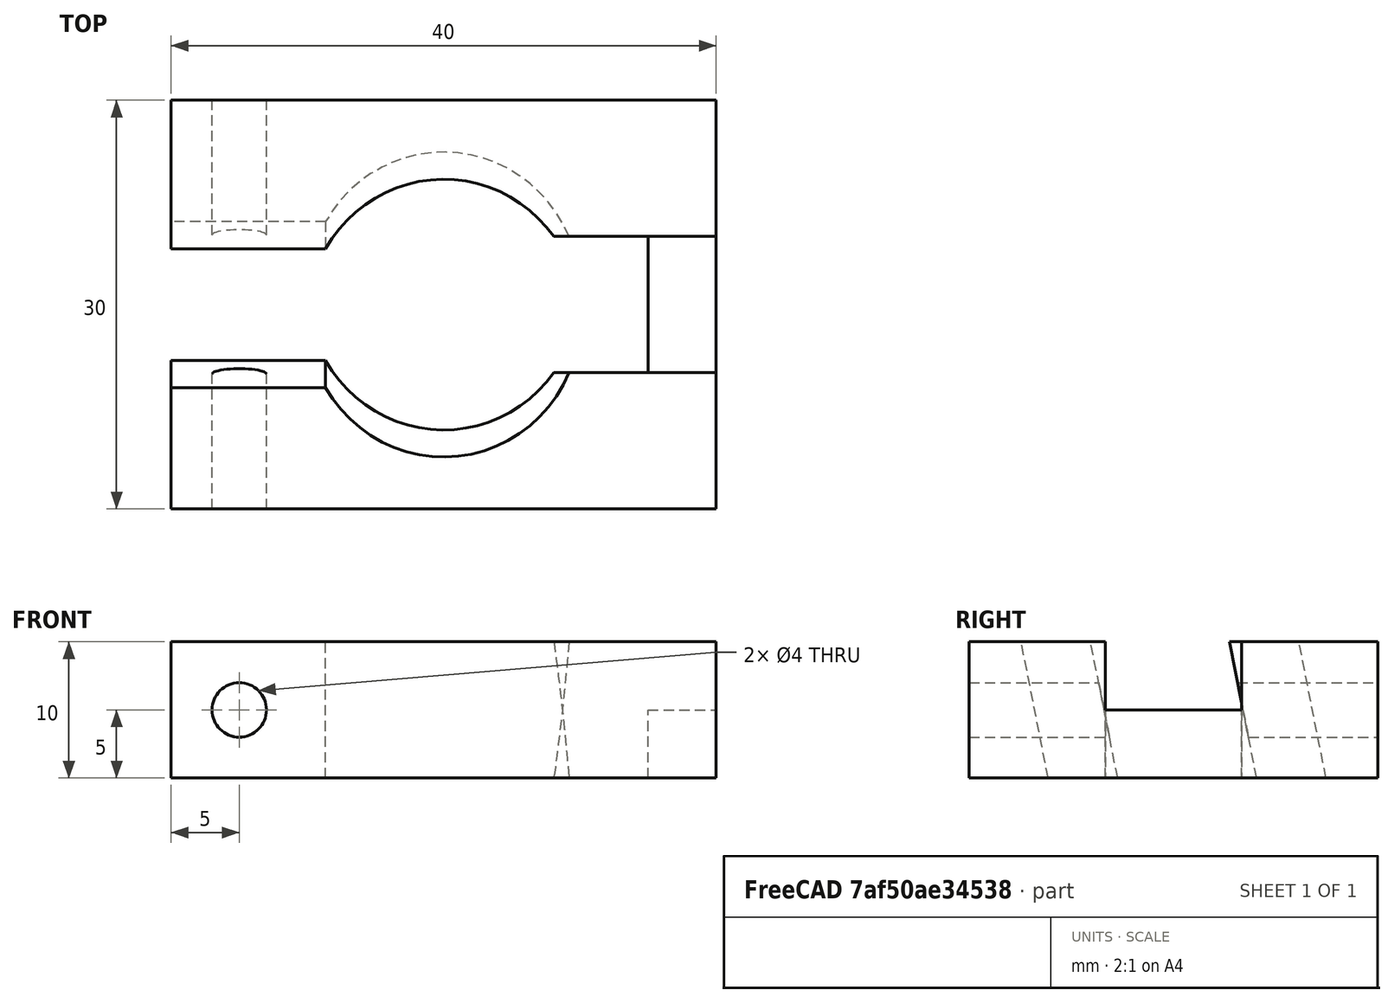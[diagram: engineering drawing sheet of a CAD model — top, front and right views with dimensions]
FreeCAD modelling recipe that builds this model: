
FCSTD DOCUMENT  (FreeCAD 0.17R13522 (Git))
Label: fastener-middleturn-rev-20mm
License: All rights reserved
LicenseURL: http://en.wikipedia.org/wiki/All_rights_reserved
objects: Part::Box×4, Part::Cylinder×2, Part::MultiFuse×2, Part::Cut×1
note: 9 computed .brp shape members not serialized (recipe doc carries the construction recipe); baked Part::Feature solids carry a one-line shape summary decoded from their .brp

FEATURE [Part::Box] Box  label="Cube"
  AttacherType = Attacher::AttachEngine3D
  Height = 10
  Length = 40
  Placement = pos=(-20,-15,-5) rot=(0,0,1;0rad)
  Width = 30
FEATURE [Part::Box] Box001  label="Cube001"
  AttacherType = Attacher::AttachEngine3D
  Height = 10
  Length = 10
  Placement = pos=(5,-5,-5) rot=(0,0,1;0rad)
  Width = 10
FEATURE [Part::Box] Box002  label="Cube002"
  AttacherType = Attacher::AttachEngine3D
  Height = 5
  Length = 10
  Placement = pos=(10,-5,0) rot=(0,0,1;0rad)
  Width = 10
FEATURE [Part::Cylinder] Cylinder003
  Angle = 360
  AttacherType = Attacher::AttachEngine3D
  Height = 30
  Placement = pos=(-15,-15,0) rot=(-1,0,0;1.5708rad)
  Radius = 2
FEATURE [Part::Box] Box003  label="Squeeze Cube"
  AttacherType = Attacher::AttachEngine3D
  Height = 20
  Length = 15
  Placement = pos=(-20,-5,-10) rot=(0,0,1;0rad)
  Width = 10
FEATURE [Part::Cylinder] Cylinder004  label="Rail Cylinder"
  Angle = 360
  AttacherType = Attacher::AttachEngine3D
  Height = 20
  Placement = pos=(0,0,-10) rot=(0,0,1;0rad)
  Radius = 10
FEATURE [Part::MultiFuse] Fusion001
  Placement = pos=(0,0,0) rot=(1,0,0;0.19635rad)
  Shapes = -> [Box003,Cylinder004]
FEATURE [Part::MultiFuse] Fusion  label="Negative Fusion"
  Shapes = -> [Box001,Box002,Cylinder003,Fusion001]
FEATURE [Part::Cut] Cut
  Base = -> Box
  Tool = -> Fusion
